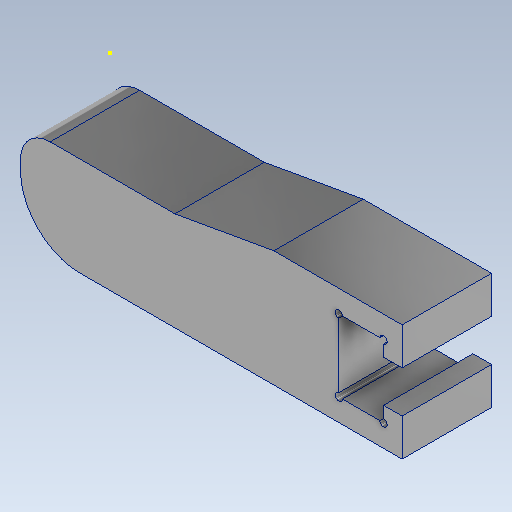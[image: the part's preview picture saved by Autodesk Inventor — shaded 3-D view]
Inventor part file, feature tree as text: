
AUTODESK INVENTOR PART (.ipt)
format: ipt  version: 2025.2 (Build 292293000, 293)  size: 347,648 bytes
history: native  units: mm
features: sketch x3, extrude x2, fillet x2
ambient origin geometry x8: Origin, YZ Plane, XZ Plane, XY Plane, X Axis, Y Axis, Z Axis, Center Point
bodies: Solid2 (feature_tree)
feature tree (7):
  extrude  "Extrusion2"  Depth=2.5mm
  extrude  "Extrusion7"  Depth=15.6mm
  fillet  "Rundung4"  Radius=5.6mm
  sketch  "Skizze13"  dims[d99=1.0mm d100=1.0mm d101=1.0mm d102=1.0mm d103=0.0mm d104=0.0mm d111=8.0mm d122=14.237mm d123=2.975mm d132=1.745329mm d133=4.0mm d131=0.0mm d134=0.0mm]
  fillet  "Rundung7"  Radius=9.65mm
  sketch  "Sketch5"  dims[d41=6.0mm d50=2.5mm]
  sketch  "Sketch11"  dims[d56=12.0mm d57=0.0mm d67=15.6mm d87=5.6mm d88=9.65mm]
